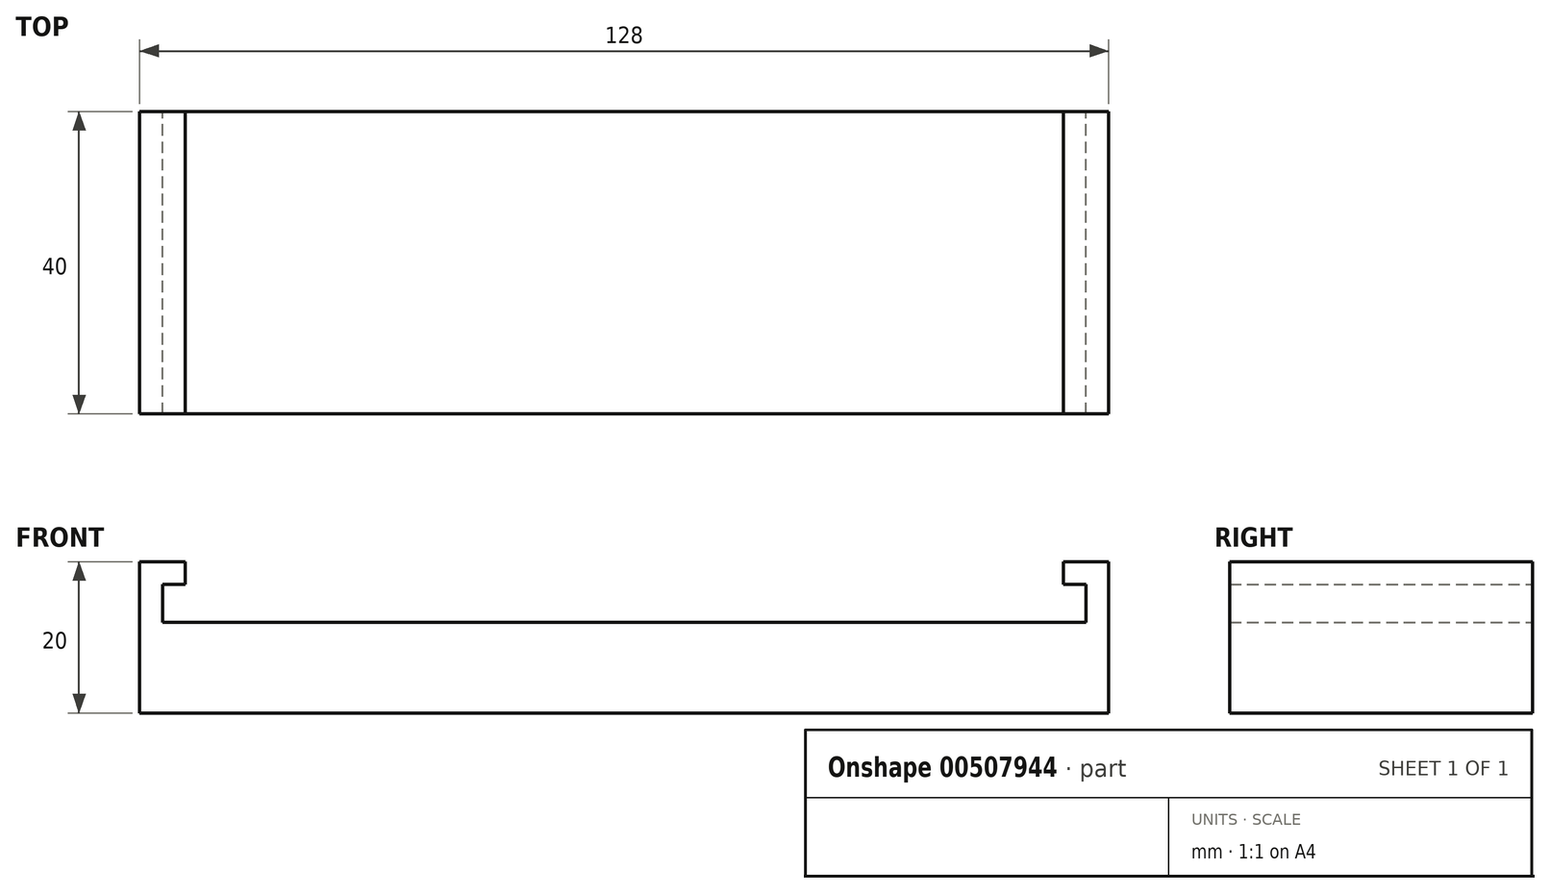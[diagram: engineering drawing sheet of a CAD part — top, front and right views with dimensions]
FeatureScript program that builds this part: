
annotation { "Feature Type Name" : "Feature", "Feature Type Description" : "" }
export const myFeature = defineFeature(function(context is Context, id is Id, definition is map)
    precondition{}
    {
        {
            var Q0;
            Q0=qCreatedBy(makeId("Front.planeOp"),FACE);
            var sketch = newSketch(context, id + "F0", { "sketchPlane" : qUnion([Q0])});
            skLineSegment(sketch, "E0", {"start": v(-65.83, -26.95) * mm, "end": v(62.17, -26.95) * mm});
            skLineSegment(sketch, "E1", {"start": v(62.17, -26.95) * mm, "end": v(62.17, -6.95) * mm});
            skLineSegment(sketch, "E2", {"start": v(62.17, -6.95) * mm, "end": v(56.17, -6.95) * mm});
            skLineSegment(sketch, "E3", {"start": v(56.17, -6.95) * mm, "end": v(56.17, -9.95) * mm});
            skLineSegment(sketch, "E4", {"start": v(56.17, -9.95) * mm, "end": v(59.17, -9.95) * mm});
            skLineSegment(sketch, "E5", {"start": v(59.17, -9.95) * mm, "end": v(59.17, -14.95) * mm});
            skLineSegment(sketch, "E6", {"start": v(59.17, -14.95) * mm, "end": v(-62.83, -14.95) * mm});
            skLineSegment(sketch, "E7", {"start": v(-62.83, -14.95) * mm, "end": v(-62.83, -9.95) * mm});
            skLineSegment(sketch, "E8", {"start": v(-62.83, -9.95) * mm, "end": v(-59.83, -9.95) * mm});
            skLineSegment(sketch, "E9", {"start": v(-59.83, -9.95) * mm, "end": v(-59.83, -6.95) * mm});
            skLineSegment(sketch, "E10", {"start": v(-59.83, -6.95) * mm, "end": v(-65.83, -6.95) * mm});
            skLineSegment(sketch, "E11", {"start": v(-65.83, -6.95) * mm, "end": v(-65.83, -26.95) * mm});
            skSolve(sketch);
        }
        {
            var Q0;
            Q0 = qSketchRegion(id + "F0", true);
            extrude(context, id + "F1", {"entities" : qUnion([Q0]), "depth" : 40 * mm});
        }
    });
